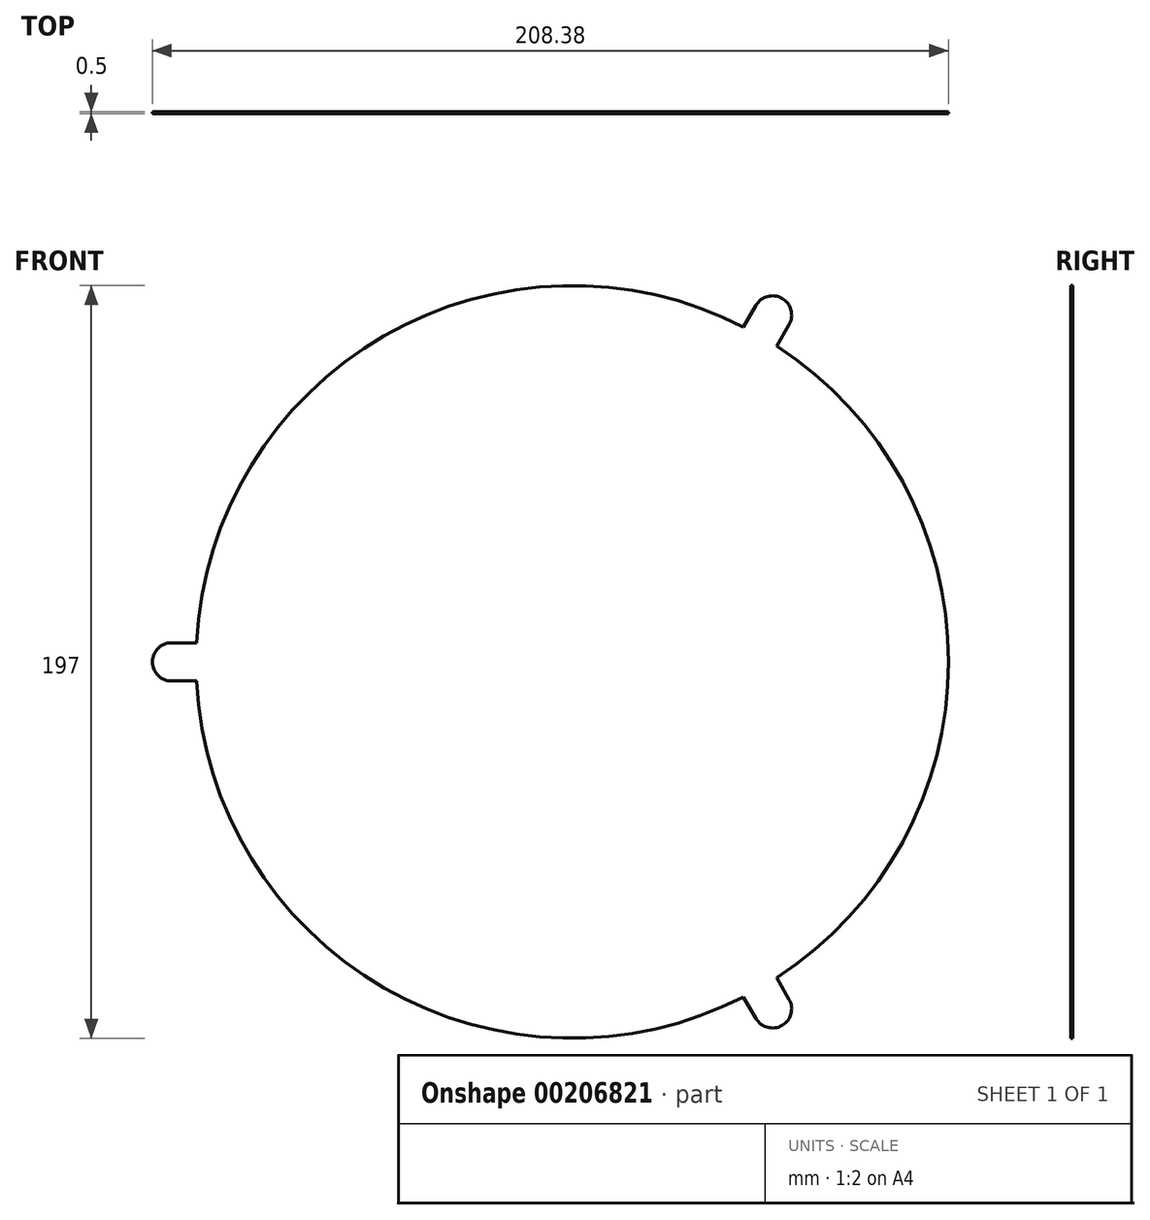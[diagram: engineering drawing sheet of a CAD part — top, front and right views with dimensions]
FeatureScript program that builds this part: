
annotation { "Feature Type Name" : "Feature", "Feature Type Description" : "" }
export const myFeature = defineFeature(function(context is Context, id is Id, definition is map)
    precondition{}
    {
        {
            var Q0;
            Q0=qCreatedBy(makeId("Front.planeOp"),FACE);
            var sketch = newSketch(context, id + "F0", { "sketchPlane" : qUnion([Q0])});
            skArc(sketch, "E0", {"start": v(-98.37, -5) * mm, "mid": v(-49.25, -85.3) * mm, "end": v(44.86, -87.7) * mm});
            skLineSegment(sketch, "E1", {"start": v(0, 0) * mm, "end": v(63.3, 109.65) * mm, "construction": true});
            skLineSegment(sketch, "E2", {"start": v(0, 0) * mm, "end": v(70.88, -122.77) * mm, "construction": true});
            skLineSegment(sketch, "E3", {"start": v(0, 0) * mm, "end": v(-175.52, 0) * mm, "construction": true});
            skCircle(sketch, "E4", {"center": v(0, 0) * mm, "radius": 105 * mm, "construction": true});
            skLineSegment(sketch, "E5", {"start": v(-98.37, 5) * mm, "end": v(-104.88, 5) * mm});
            skLineSegment(sketch, "E6.MirrorCS", {"start": v(-98.37, -5) * mm, "end": v(-104.88, -5) * mm});
            skArc(sketch, "E7", {"start": v(-104.88, 5) * mm, "mid": v(-109.88, 0) * mm, "end": v(-104.88, -5) * mm});
            skLineSegment(sketch, "E8.1.0", {"start": v(44.86, -87.7) * mm, "end": v(48.11, -93.33) * mm});
            skLineSegment(sketch, "E8.1.1", {"start": v(53.52, -82.7) * mm, "end": v(56.77, -88.33) * mm});
            skArc(sketch, "E8.1.2", {"start": v(48.11, -93.33) * mm, "mid": v(54.94, -95.16) * mm, "end": v(56.77, -88.33) * mm});
            skLineSegment(sketch, "E8.2.0", {"start": v(53.52, 82.7) * mm, "end": v(56.77, 88.33) * mm});
            skLineSegment(sketch, "E8.2.1", {"start": v(44.86, 87.7) * mm, "end": v(48.11, 93.33) * mm});
            skArc(sketch, "E8.2.2", {"start": v(56.77, 88.33) * mm, "mid": v(54.94, 95.16) * mm, "end": v(48.11, 93.33) * mm});
            skArc(sketch, "E9.trimOffspring", {"start": v(53.52, -82.7) * mm, "mid": v(98.5, 0) * mm, "end": v(53.52, 82.7) * mm});
            skArc(sketch, "E10.trimOffspring", {"start": v(44.86, 87.7) * mm, "mid": v(-49.25, 85.3) * mm, "end": v(-98.37, 5) * mm});
            skSolve(sketch);
        }
        {
            var Q0;
            Q0 = qSketchRegion(id + "F0", true);
            extrude(context, id + "F1", {"entities" : qUnion([Q0]), "depth" : 0.5 * mm});
        }
    });
